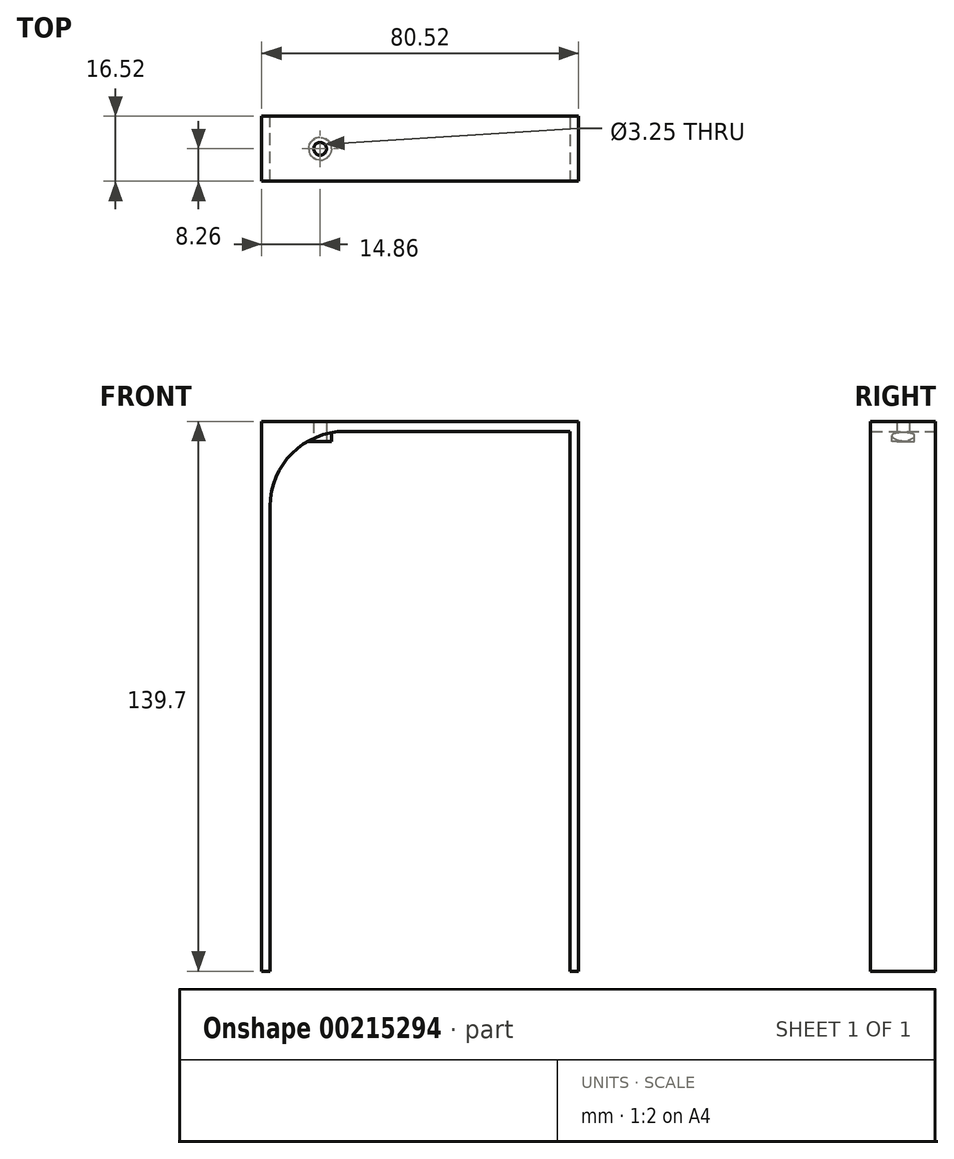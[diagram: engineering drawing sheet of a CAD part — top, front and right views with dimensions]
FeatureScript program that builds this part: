
annotation { "Feature Type Name" : "Feature", "Feature Type Description" : "" }
export const myFeature = defineFeature(function(context is Context, id is Id, definition is map)
    precondition{}
    {
        {
            var Q0;
            Q0=qCreatedBy(makeId("Top.planeOp"),FACE);
            var sketch = newSketch(context, id + "F0", { "sketchPlane" : qUnion([Q0])});
            skLineSegment(sketch, "E0.bottom", {"start": v(-40.26, 8.25) * mm, "end": v(40.26, 8.25) * mm});
            skLineSegment(sketch, "E0.top", {"start": v(-40.26, -8.26) * mm, "end": v(40.26, -8.26) * mm});
            skLineSegment(sketch, "E0.left", {"start": v(-40.26, 8.25) * mm, "end": v(-40.26, -8.26) * mm});
            skLineSegment(sketch, "E0.right", {"start": v(40.26, 8.25) * mm, "end": v(40.26, -8.26) * mm});
            skSolve(sketch);
        }
        {
            var Q0;
            Q0 = qSketchRegion(id + "F0", true);
            extrude(context, id + "F1", {"entities" : qUnion([Q0]), "depth" : 2.54 * mm});
        }
        {
            var Q0;
            Q0=makeQuery(id+"F1.opExtrude","CAP_FACE",FACE,{"disambiguationData":[OSD([sQuery(id+"F0.wireOp",EDGE,"E0.bottom"),sQuery(id+"F0.wireOp",EDGE,"E0.top"),sQuery(id+"F0.wireOp",EDGE,"E0.left"),sQuery(id+"F0.wireOp",EDGE,"E0.right")])],"isStart":false});
            var sketch = newSketch(context, id + "F2", { "sketchPlane" : qUnion([Q0])});
            skLineSegment(sketch, "E1.bottom", {"start": v(-40.26, 8.25) * mm, "end": v(-38.1, 8.25) * mm});
            skLineSegment(sketch, "E1.top", {"start": v(-40.26, -8.26) * mm, "end": v(-38.1, -8.26) * mm});
            skLineSegment(sketch, "E1.left", {"start": v(-40.26, 8.25) * mm, "end": v(-40.26, -8.26) * mm});
            skLineSegment(sketch, "E1.right", {"start": v(-38.1, 8.25) * mm, "end": v(-38.1, -8.26) * mm});
            skLineSegment(sketch, "E2.bottom", {"start": v(40.26, 8.25) * mm, "end": v(38.1, 8.25) * mm});
            skLineSegment(sketch, "E2.top", {"start": v(40.26, -8.26) * mm, "end": v(38.1, -8.26) * mm});
            skLineSegment(sketch, "E2.left", {"start": v(40.26, 8.25) * mm, "end": v(40.26, -8.26) * mm});
            skLineSegment(sketch, "E2.right", {"start": v(38.1, 8.25) * mm, "end": v(38.1, -8.26) * mm});
            skSolve(sketch);
        }
        {
            var Q0;
            Q0 = qSketchRegion(id + "F2", true);
            extrude(context, id + "F3", {"entities" : qUnion([Q0]), "operationType" : NewBodyOperationType.ADD, "oppositeDirection" : true, "depth" : 139.7 * mm});
        }
        {
            var Q0;
            Q0=makeQuery(id+"F3.boolean.opBoolean","MERGE",FACE,{"derivedFrom":[makeQuery(id+"F1.opExtrude","SWEPT_FACE",FACE,{"disambiguationData":[OSD([sQuery(id+"F0.wireOp",EDGE,"E0.bottom")])]}),makeQuery(id+"F3.opExtrude","SWEPT_FACE",FACE,{"disambiguationData":[OSD([sQuery(id+"F2.wireOp",EDGE,"E1.bottom")])]}),makeQuery(id+"F3.opExtrude","SWEPT_FACE",FACE,{"disambiguationData":[OSD([sQuery(id+"F2.wireOp",EDGE,"E2.bottom")])]})]});
            var sketch = newSketch(context, id + "F4", { "sketchPlane" : qUnion([Q0])});
            skLineSegment(sketch, "E3", {"start": v(38.1, 0) * mm, "end": v(19.05, 0) * mm});
            skLineSegment(sketch, "E4", {"start": v(38.1, 0) * mm, "end": v(38.1, -19.05) * mm});
            skArc(sketch, "E5", {"start": v(38.1, -19.05) * mm, "mid": v(32.52, -5.58) * mm, "end": v(19.05, 0) * mm});
            skSolve(sketch);
        }
        {
            var Q0;
            Q0 = qSketchRegion(id + "F4", true);
            var Q1;
            Q1=makeQuery(id+"F3.boolean.opBoolean","MERGE",FACE,{"derivedFrom":[makeQuery(id+"F1.opExtrude","SWEPT_FACE",FACE,{"disambiguationData":[OSD([sQuery(id+"F0.wireOp",EDGE,"E0.top")])]}),makeQuery(id+"F3.opExtrude","SWEPT_FACE",FACE,{"disambiguationData":[OSD([sQuery(id+"F2.wireOp",EDGE,"E1.top")])]}),makeQuery(id+"F3.opExtrude","SWEPT_FACE",FACE,{"disambiguationData":[OSD([sQuery(id+"F2.wireOp",EDGE,"E2.top")])]})]});
            extrude(context, id + "F5", {"entities" : qUnion([Q0]), "operationType" : NewBodyOperationType.ADD, "endBound" : BoundingType.UP_TO_SURFACE, "oppositeDirection" : true, "endBoundEntityFace" : qUnion([Q1]), "depth" : 25.4 * mm});
        }
        {
            var Q0;
            Q0=makeQuery(id+"F1.opExtrude","CAP_FACE",FACE,{"disambiguationData":[OSD([sQuery(id+"F0.wireOp",EDGE,"E0.bottom"),sQuery(id+"F0.wireOp",EDGE,"E0.top"),sQuery(id+"F0.wireOp",EDGE,"E0.left"),sQuery(id+"F0.wireOp",EDGE,"E0.right")])],"isStart":true});
            var sketch = newSketch(context, id + "F6", { "sketchPlane" : qUnion([Q0])});
            skCircle(sketch, "E6", {"center": v(-25.4, 0) * mm, "radius": 1.63 * mm});
            skSolve(sketch);
        }
        {
            var Q0;
            Q0 = qSketchRegion(id + "F6", true);
            extrude(context, id + "F7", {"entities" : qUnion([Q0]), "operationType" : NewBodyOperationType.REMOVE, "endBound" : BoundingType.THROUGH_ALL, "oppositeDirection" : true, "depth" : 25.4 * mm, "hasSecondDirection" : true, "secondDirectionBound" : SecondDirectionBoundingType.THROUGH_ALL, "secondDirectionOppositeDirection" : false, "secondDirectionDepth" : 25.4 * mm});
        }
        {
            var Q0;
            Q0=makeQuery(id+"F1.opExtrude","CAP_FACE",FACE,{"disambiguationData":[OSD([sQuery(id+"F0.wireOp",EDGE,"E0.bottom"),sQuery(id+"F0.wireOp",EDGE,"E0.top"),sQuery(id+"F0.wireOp",EDGE,"E0.left"),sQuery(id+"F0.wireOp",EDGE,"E0.right")])],"isStart":true});
            var sketch = newSketch(context, id + "F8", { "sketchPlane" : qUnion([Q0])});
            skCircle(sketch, "E7.0", {"center": v(-25.4, 0) * mm, "radius": 1.63 * mm});
            skCircle(sketch, "E8.0", {"center": v(-25.4, 0) * mm, "radius": 2.9 * mm});
            skSolve(sketch);
        }
        {
            var Q0;
            Q0 = qSketchRegion(id + "F8", true);
            extrude(context, id + "F9", {"entities" : qUnion([Q0]), "operationType" : NewBodyOperationType.ADD, "depth" : 2.54 * mm});
        }
    });
